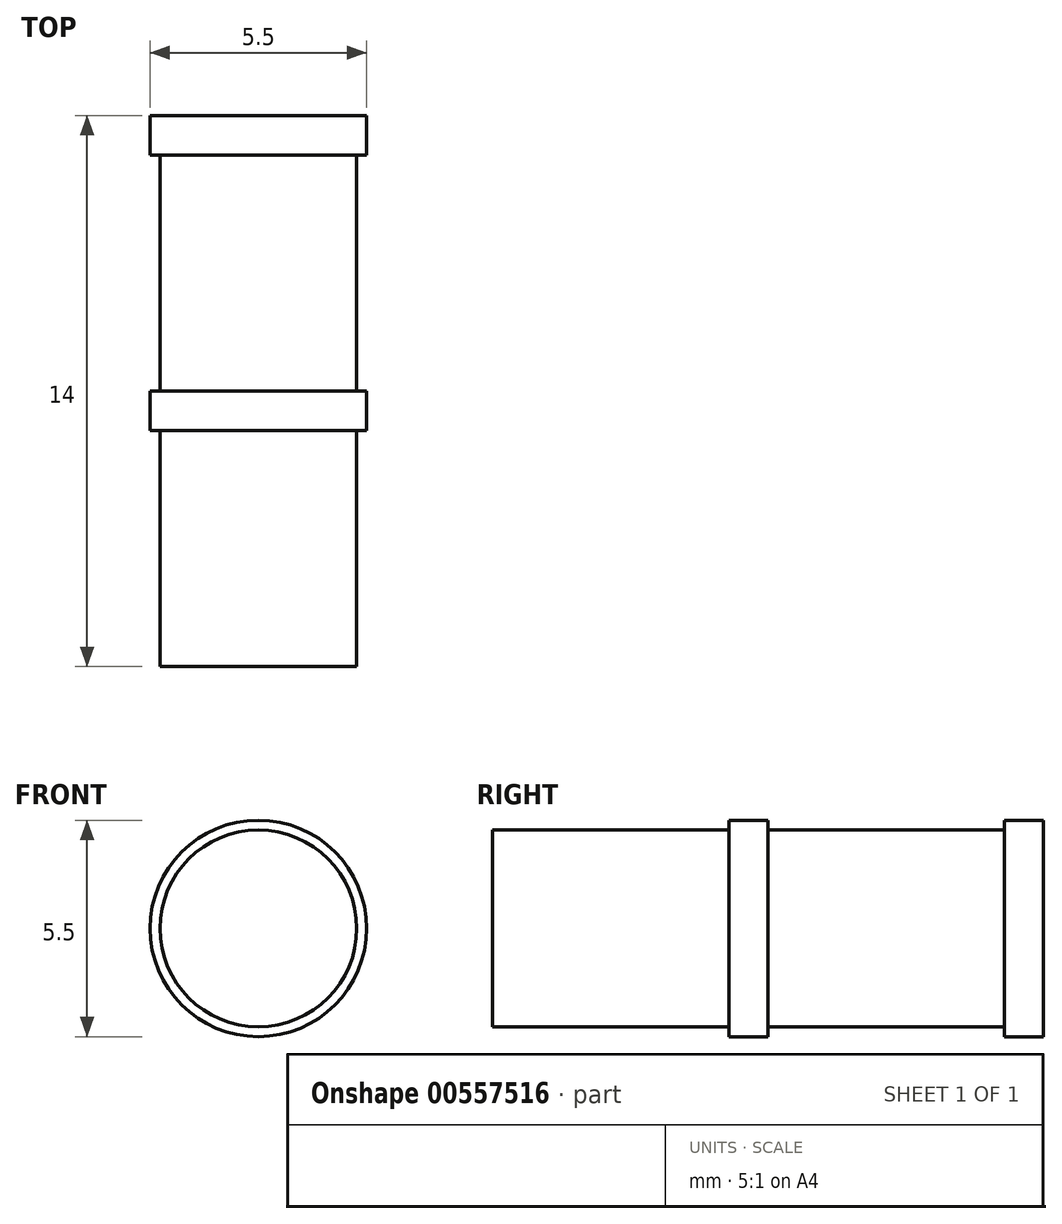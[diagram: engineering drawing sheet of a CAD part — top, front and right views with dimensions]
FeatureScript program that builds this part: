
annotation { "Feature Type Name" : "Feature", "Feature Type Description" : "" }
export const myFeature = defineFeature(function(context is Context, id is Id, definition is map)
    precondition{}
    {
        {
            var Q0;
            Q0=qCreatedBy(makeId("Front.planeOp"),FACE);
            var sketch = newSketch(context, id + "F0", { "sketchPlane" : qUnion([Q0])});
            skCircle(sketch, "E0", {"center": v(0, 0) * mm, "radius": 2.75 * mm});
            skSolve(sketch);
        }
        {
            var Q0;
            Q0 = qSketchRegion(id + "F0", true);
            extrude(context, id + "F1", {"entities" : qUnion([Q0]), "endBound" : BoundingType.SYMMETRIC, "depth" : 14 * mm, "offsetDistance" : 25 * mm});
        }
        {
            var Q0;
            Q0=makeQuery(id+"F1.opExtrude","CAP_FACE",FACE,{"disambiguationData":[OSD([sQuery(id+"F0.wireOp",EDGE,"E0")])],"isStart":false});
            var sketch = newSketch(context, id + "F2", { "sketchPlane" : qUnion([Q0])});
            skCircle(sketch, "E1", {"center": v(0, 0) * mm, "radius": 2.75 * mm});
            skCircle(sketch, "E2", {"center": v(0, 0) * mm, "radius": 2.5 * mm});
            skSolve(sketch);
        }
        {
            var Q0;
            Q0=makeQuery(id+"F2.imprint","IMPRINT",FACE,{"disambiguationData":[TD([[makeQuery(id+"F2.imprint","IMPRINT",EDGE,{"derivedFrom":sQuery(id+"F2.wireOp",EDGE,"E1")}),1.0]])]});
            extrude(context, id + "F3", {"entities" : qUnion([Q0]), "operationType" : NewBodyOperationType.REMOVE, "oppositeDirection" : true, "depth" : 6 * mm, "offsetDistance" : 25 * mm});
        }
        {
            var Q0;
            Q0=qCreatedBy(makeId("Front.planeOp"),FACE);
            var sketch = newSketch(context, id + "F4", { "sketchPlane" : qUnion([Q0])});
            skCircle(sketch, "E3", {"center": v(0, 0) * mm, "radius": 2.5 * mm});
            skCircle(sketch, "E4", {"center": v(0, 0) * mm, "radius": 2.75 * mm});
            skSolve(sketch);
        }
        {
            var Q0;
            Q0 = qSketchRegion(id + "F4", true);
            extrude(context, id + "F5", {"entities" : qUnion([Q0]), "operationType" : NewBodyOperationType.REMOVE, "oppositeDirection" : true, "depth" : 6 * mm, "offsetDistance" : 25 * mm});
        }
    });
